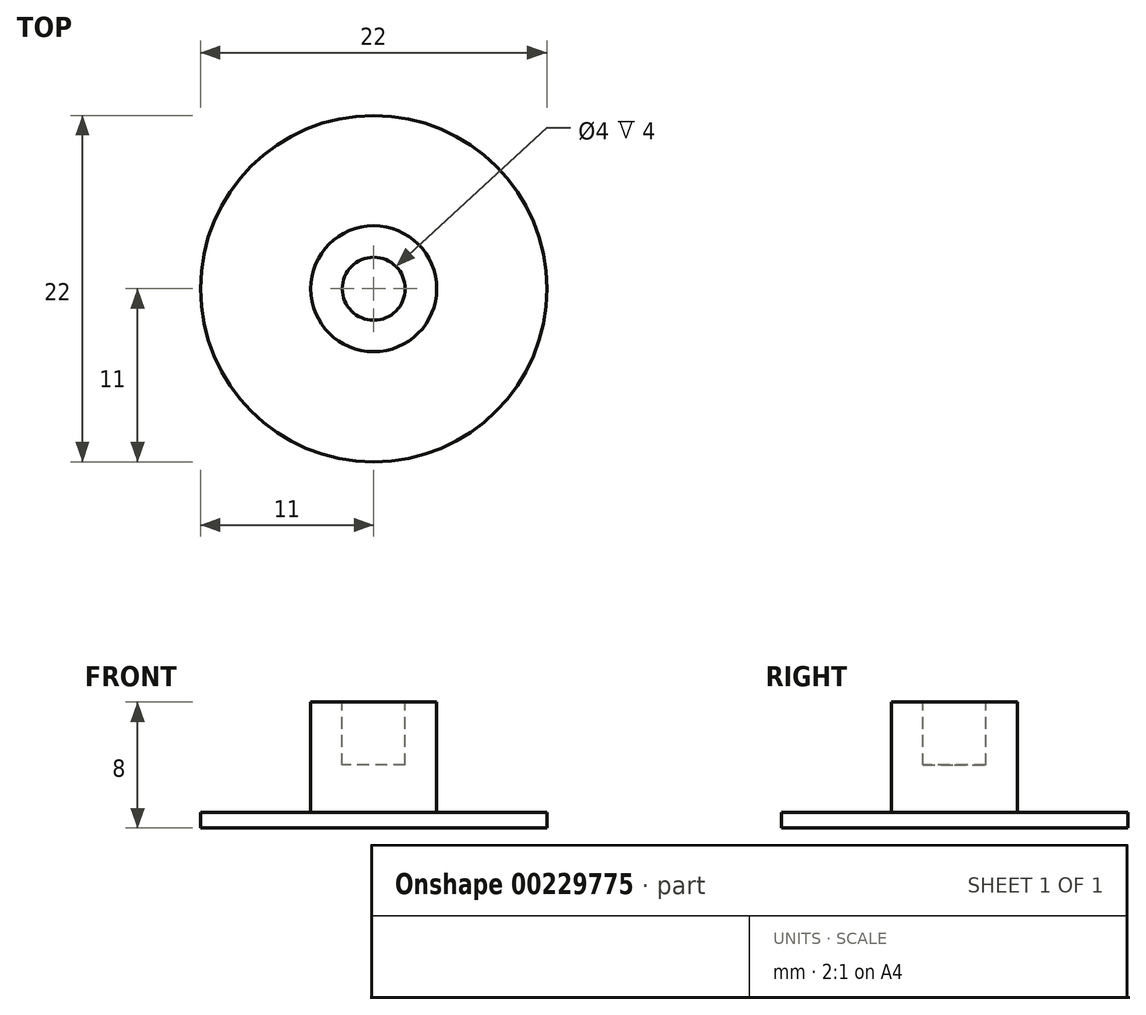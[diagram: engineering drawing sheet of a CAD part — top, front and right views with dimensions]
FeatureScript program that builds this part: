
annotation { "Feature Type Name" : "Feature", "Feature Type Description" : "" }
export const myFeature = defineFeature(function(context is Context, id is Id, definition is map)
    precondition{}
    {
        {
            var Q0;
            Q0=qCreatedBy(makeId("Top.planeOp"),FACE);
            var sketch = newSketch(context, id + "F0", { "sketchPlane" : qUnion([Q0])});
            skCircle(sketch, "E0", {"center": v(0, 0) * mm, "radius": 11 * mm});
            skCircle(sketch, "E1", {"center": v(0, 0) * mm, "radius": 4 * mm});
            skSolve(sketch);
        }
        {
            var Q0;
            Q0=makeQuery(id+"F0.imprint","IMPRINT",FACE,{"disambiguationData":[TD([[makeQuery(id+"F0.imprint","IMPRINT",EDGE,{"derivedFrom":sQuery(id+"F0.wireOp",EDGE,"E0")}),1.0]])]});
            var Q1;
            Q1=makeQuery(id+"F0.imprint","IMPRINT",FACE,{"disambiguationData":[TD([[makeQuery(id+"F0.imprint","IMPRINT",EDGE,{"derivedFrom":sQuery(id+"F0.wireOp",EDGE,"E1")}),1.0]])]});
            extrude(context, id + "F1", {"entities" : qUnion([Q0, Q1]), "depth" : 1 * mm, "offsetDistance" : 25.4 * mm});
        }
        {
            var Q0;
            Q0=makeQuery(id+"F1.opExtrude","CAP_FACE",FACE,{"disambiguationData":[OSD([sQuery(id+"F0.wireOp",EDGE,"E0"),sQuery(id+"F0.wireOp",EDGE,"E1")])],"isStart":false});
            var sketch = newSketch(context, id + "F2", { "sketchPlane" : qUnion([Q0])});
            skCircle(sketch, "E2", {"center": v(0, 0) * mm, "radius": 4 * mm});
            skSolve(sketch);
        }
        {
            var Q0;
            Q0 = qSketchRegion(id + "F2", true);
            extrude(context, id + "F3", {"entities" : qUnion([Q0]), "depth" : 7 * mm, "offsetDistance" : 25.4 * mm});
        }
        {
            var Q0;
            Q0=makeQuery(id+"F3.opExtrude","CAP_FACE",FACE,{"disambiguationData":[OSD([sQuery(id+"F2.wireOp",EDGE,"E2")])],"isStart":false});
            var sketch = newSketch(context, id + "F4", { "sketchPlane" : qUnion([Q0])});
            skCircle(sketch, "E3", {"center": v(0, 0) * mm, "radius": 2 * mm});
            skSolve(sketch);
        }
        {
            var Q0;
            Q0 = qSketchRegion(id + "F4", true);
            extrude(context, id + "F5", {"entities" : qUnion([Q0]), "operationType" : NewBodyOperationType.REMOVE, "oppositeDirection" : true, "depth" : 4 * mm, "offsetDistance" : 25.4 * mm});
        }
    });
